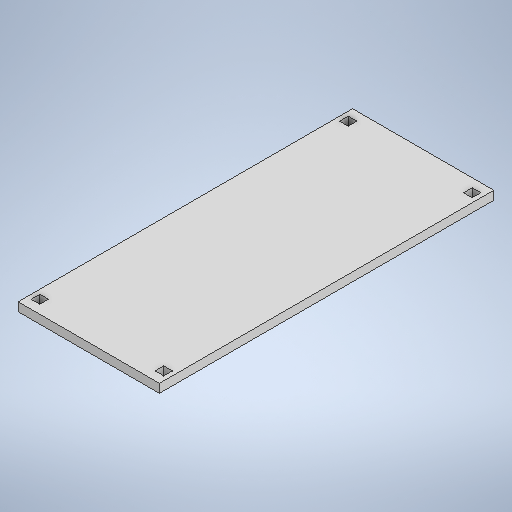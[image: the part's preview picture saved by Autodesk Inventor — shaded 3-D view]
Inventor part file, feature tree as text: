
AUTODESK INVENTOR PART (.ipt)
format: ipt  version: 2025 (Build 290162000, 162)  size: 262,144 bytes
history: native  units: in
note: dims shown in document units (in); Inventor stores cm internally (conversion verified against a paired STEP export)
features: extrude x2, sketch x2
ambient origin geometry x8: Origin, YZ Plane, XZ Plane, XY Plane, X Axis, Y Axis, Z Axis, Center Point
bodies: Solid1 (feature_tree)
feature tree (4):
  extrude  "Extrusion1"  Depth=19.2913in
  extrude  "Extrusion2"  Depth=1.1811in
  sketch  "Sketch1"  dims[d0=45.6693in d1=19.2913in]
  sketch  "Sketch2"  dims[d2=1.1811in d3=1.1811in d4=0.5906in d5=1.1811in d6=1.1811in d7=0.5906in d8=1.1811in d9=0.5906in d10=1.1811in d11=1.1811in d12=0.5906in d13=1.1811in d14=1.1811in d15=0.0in d16=25.5906in d17=11.811in d18=1.1811in d19=0.0in]
